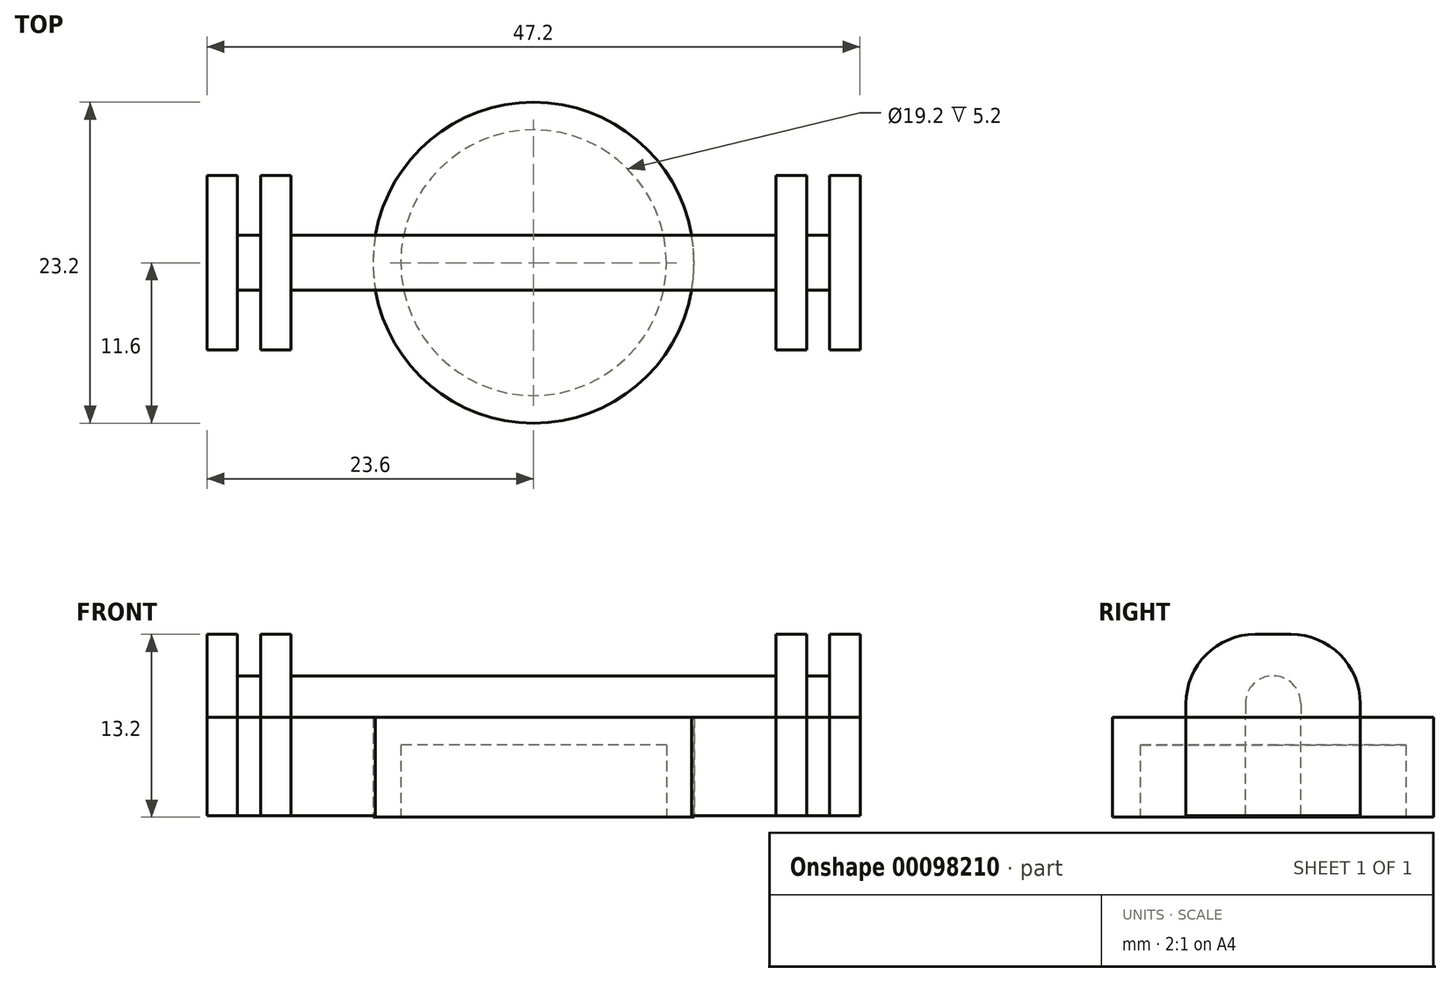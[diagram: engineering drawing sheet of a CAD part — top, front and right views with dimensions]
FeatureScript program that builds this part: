
annotation { "Feature Type Name" : "Feature", "Feature Type Description" : "" }
export const myFeature = defineFeature(function(context is Context, id is Id, definition is map)
    precondition{}
    {
        {
            var Q0;
            Q0=qCreatedBy(makeId("Top.planeOp"),FACE);
            var sketch = newSketch(context, id + "F0", { "sketchPlane" : qUnion([Q0])});
            skCircle(sketch, "E0", {"center": v(0, 0) * mm, "radius": 9.6 * mm});
            skCircle(sketch, "E1.0", {"center": v(0, 0) * mm, "radius": 11.6 * mm});
            skSolve(sketch);
        }
        {
            var Q0;
            Q0 = qSketchRegion(id + "F0", true);
            extrude(context, id + "F1", {"entities" : qUnion([Q0]), "depth" : 5.2 * mm});
        }
        {
            var Q0;
            Q0=makeQuery(id+"F1.opExtrude","CAP_FACE",FACE,{"disambiguationData":[OSD([sQuery(id+"F0.wireOp",EDGE,"E0"),sQuery(id+"F0.wireOp",EDGE,"E1.0")])],"isStart":false});
            var sketch = newSketch(context, id + "F2", { "sketchPlane" : qUnion([Q0])});
            skSolve(sketch);
        }
        {
            var Q0;
            Q0=makeQuery(id+"F2.imprint","IMPRINT",FACE,{"disambiguationData":[TD([[makeQuery(id+"F2.imprint","IMPRINT",EDGE,{"derivedFrom":makeQuery(id+"F1.opExtrude","CAP_EDGE",EDGE,{"disambiguationData":[OSD([sQuery(id+"F0.wireOp",EDGE,"E0")])],"isStart":false})}),1.0]])]});
            var Q1;
            Q1=makeQuery(id+"F2.imprint","IMPRINT",FACE,{"disambiguationData":[TD([[makeQuery(id+"F2.imprint","IMPRINT",EDGE,{"derivedFrom":makeQuery(id+"F1.opExtrude","CAP_EDGE",EDGE,{"disambiguationData":[OSD([sQuery(id+"F0.wireOp",EDGE,"E0")])],"isStart":false})}),-1.0]])]});
            extrude(context, id + "F3", {"entities" : qUnion([Q0, Q1]), "operationType" : NewBodyOperationType.ADD, "depth" : 2 * mm});
        }
        {
            var Q0;
            Q0=makeQuery(id+"F3.opExtrude","CAP_FACE",FACE,{"disambiguationData":[OSD([sQuery(id+"F0.wireOp",EDGE,"E1.0")])],"isStart":false});
            var sketch = newSketch(context, id + "F4", { "sketchPlane" : qUnion([Q0])});
            skLineSegment(sketch, "E2.bottom", {"start": v(-22.5, 2) * mm, "end": v(22.5, 2) * mm});
            skLineSegment(sketch, "E2.top", {"start": v(-22.5, -2) * mm, "end": v(22.5, -2) * mm});
            skLineSegment(sketch, "E2.left", {"start": v(-22.5, 2) * mm, "end": v(-22.5, -2) * mm});
            skLineSegment(sketch, "E2.right", {"start": v(22.5, 2) * mm, "end": v(22.5, -2) * mm});
            skPoint(sketch, "E2.middle", {"position": v(0, 0) * mm});
            skLineSegment(sketch, "E3.bottom", {"start": v(-21.4, -6.3) * mm, "end": v(-23.6, -6.3) * mm});
            skLineSegment(sketch, "E3.top", {"start": v(-21.4, 6.3) * mm, "end": v(-23.6, 6.3) * mm});
            skLineSegment(sketch, "E3.left", {"start": v(-21.4, -6.3) * mm, "end": v(-21.4, 6.3) * mm});
            skLineSegment(sketch, "E3.right", {"start": v(-23.6, -6.3) * mm, "end": v(-23.6, 6.3) * mm});
            skPoint(sketch, "E3.middle", {"position": v(-22.5, 0) * mm});
            skLineSegment(sketch, "E4.bottom", {"start": v(-17.53, 6.3) * mm, "end": v(-19.74, 6.3) * mm});
            skLineSegment(sketch, "E4.top", {"start": v(-17.53, -6.3) * mm, "end": v(-19.74, -6.3) * mm});
            skLineSegment(sketch, "E4.left", {"start": v(-17.53, 6.3) * mm, "end": v(-17.53, -6.3) * mm});
            skLineSegment(sketch, "E4.right", {"start": v(-19.74, 6.3) * mm, "end": v(-19.74, -6.3) * mm});
            skPoint(sketch, "E4.middle", {"position": v(-18.63, 0) * mm});
            skLineSegment(sketch, "E5.MirrorCS", {"start": v(23.6, -6.3) * mm, "end": v(23.6, 6.3) * mm});
            skLineSegment(sketch, "E6.MirrorCS", {"start": v(21.4, 6.3) * mm, "end": v(23.6, 6.3) * mm});
            skLineSegment(sketch, "E7.MirrorCS", {"start": v(21.4, -6.3) * mm, "end": v(21.4, 6.3) * mm});
            skLineSegment(sketch, "E8.MirrorCS", {"start": v(21.4, -6.3) * mm, "end": v(23.6, -6.3) * mm});
            skLineSegment(sketch, "E9.MirrorCS", {"start": v(19.74, 6.3) * mm, "end": v(19.74, -6.3) * mm});
            skLineSegment(sketch, "E10.MirrorCS", {"start": v(17.53, 6.3) * mm, "end": v(17.53, -6.3) * mm});
            skLineSegment(sketch, "E11.MirrorCS", {"start": v(17.53, -6.3) * mm, "end": v(19.74, -6.3) * mm});
            skLineSegment(sketch, "E12.MirrorCS", {"start": v(17.53, 6.3) * mm, "end": v(19.74, 6.3) * mm});
            skSolve(sketch);
        }
        {
            var Q0;
            {var subQ0=sQuery(id+"F4.wireOp",EDGE,"E4.left");var subQ1=sQuery(id+"F4.wireOp",EDGE,"E2.bottom");var subQ2=makeQuery(id+"F4.imprint","INTERSECT",VERTEX,{"derivedFrom":[subQ1,subQ0]});Q0=makeQuery(id+"F4.imprint","IMPRINT",FACE,{"disambiguationData":[TD([[makeQuery(id+"F4.imprint","IMPRINT",EDGE,{"disambiguationData":[TD([[subQ2,-1.0]])],"derivedFrom":subQ1}),-1.0]])]});}
            var Q1;
            {var subQ0=sQuery(id+"F4.wireOp",EDGE,"E4.right");var subQ1=sQuery(id+"F4.wireOp",EDGE,"E2.bottom");var subQ2=makeQuery(id+"F4.imprint","INTERSECT",VERTEX,{"derivedFrom":[subQ1,subQ0]});Q1=makeQuery(id+"F4.imprint","IMPRINT",FACE,{"disambiguationData":[TD([[makeQuery(id+"F4.imprint","IMPRINT",EDGE,{"disambiguationData":[TD([[subQ2,-1.0]])],"derivedFrom":subQ1}),-1.0]])]});}
            var Q2;
            {var subQ5=sQuery(id+"F4.wireOp",EDGE,"E4.top");Q2=makeQuery(id+"F4.imprint","IMPRINT",FACE,{"disambiguationData":[TD([[makeQuery(id+"F4.imprint","IMPRINT",EDGE,{"derivedFrom":subQ5}),-1.0]])]});}
            var Q3;
            {var subQ1=sQuery(id+"F4.wireOp",EDGE,"E2.left");Q3=makeQuery(id+"F4.imprint","IMPRINT",FACE,{"disambiguationData":[TD([[makeQuery(id+"F4.imprint","IMPRINT",EDGE,{"derivedFrom":subQ1}),-1.0]])]});}
            var Q4;
            {var subQ0=sQuery(id+"F4.wireOp",EDGE,"E2.left");Q4=makeQuery(id+"F4.imprint","IMPRINT",FACE,{"disambiguationData":[TD([[makeQuery(id+"F4.imprint","IMPRINT",EDGE,{"derivedFrom":subQ0}),1.0]])]});}
            var Q5;
            {var subQ5=sQuery(id+"F4.wireOp",EDGE,"E4.bottom");Q5=makeQuery(id+"F4.imprint","IMPRINT",FACE,{"disambiguationData":[TD([[makeQuery(id+"F4.imprint","IMPRINT",EDGE,{"derivedFrom":subQ5}),1.0]])]});}
            var Q6;
            {var subQ0=sQuery(id+"F4.wireOp",EDGE,"E3.left");var subQ1=sQuery(id+"F4.wireOp",EDGE,"E2.bottom");var subQ2=makeQuery(id+"F4.imprint","INTERSECT",VERTEX,{"derivedFrom":[subQ1,subQ0]});Q6=makeQuery(id+"F4.imprint","IMPRINT",FACE,{"disambiguationData":[TD([[makeQuery(id+"F4.imprint","IMPRINT",EDGE,{"disambiguationData":[TD([[subQ2,-1.0]])],"derivedFrom":subQ1}),-1.0]])]});}
            var Q7;
            {var subQ0=sQuery(id+"F4.wireOp",EDGE,"E10.MirrorCS");var subQ1=sQuery(id+"F4.wireOp",EDGE,"E2.bottom");var subQ2=makeQuery(id+"F4.imprint","INTERSECT",VERTEX,{"derivedFrom":[subQ1,subQ0]});Q7=makeQuery(id+"F4.imprint","IMPRINT",FACE,{"disambiguationData":[TD([[makeQuery(id+"F4.imprint","IMPRINT",EDGE,{"disambiguationData":[TD([[subQ2,1.0]])],"derivedFrom":subQ1}),-1.0]])]});}
            var Q8;
            {var subQ0=sQuery(id+"F4.wireOp",EDGE,"E10.MirrorCS");var subQ1=sQuery(id+"F4.wireOp",EDGE,"E2.bottom");var subQ2=makeQuery(id+"F4.imprint","INTERSECT",VERTEX,{"derivedFrom":[subQ1,subQ0]});Q8=makeQuery(id+"F4.imprint","IMPRINT",FACE,{"disambiguationData":[TD([[makeQuery(id+"F4.imprint","IMPRINT",EDGE,{"disambiguationData":[TD([[subQ2,-1.0]])],"derivedFrom":subQ1}),-1.0]])]});}
            var Q9;
            {var subQ5=sQuery(id+"F4.wireOp",EDGE,"E11.MirrorCS");Q9=makeQuery(id+"F4.imprint","IMPRINT",FACE,{"disambiguationData":[TD([[makeQuery(id+"F4.imprint","IMPRINT",EDGE,{"derivedFrom":subQ5}),1.0]])]});}
            var Q10;
            {var subQ0=sQuery(id+"F4.wireOp",EDGE,"E2.right");Q10=makeQuery(id+"F4.imprint","IMPRINT",FACE,{"disambiguationData":[TD([[makeQuery(id+"F4.imprint","IMPRINT",EDGE,{"derivedFrom":subQ0}),1.0]])]});}
            var Q11;
            {var subQ0=sQuery(id+"F4.wireOp",EDGE,"E9.MirrorCS");var subQ1=sQuery(id+"F4.wireOp",EDGE,"E2.bottom");var subQ2=makeQuery(id+"F4.imprint","INTERSECT",VERTEX,{"derivedFrom":[subQ1,subQ0]});Q11=makeQuery(id+"F4.imprint","IMPRINT",FACE,{"disambiguationData":[TD([[makeQuery(id+"F4.imprint","IMPRINT",EDGE,{"disambiguationData":[TD([[subQ2,-1.0]])],"derivedFrom":subQ1}),-1.0]])]});}
            var Q12;
            {var subQ5=sQuery(id+"F4.wireOp",EDGE,"E12.MirrorCS");Q12=makeQuery(id+"F4.imprint","IMPRINT",FACE,{"disambiguationData":[TD([[makeQuery(id+"F4.imprint","IMPRINT",EDGE,{"derivedFrom":subQ5}),-1.0]])]});}
            var Q13;
            {var subQ0=sQuery(id+"F4.wireOp",EDGE,"E2.right");Q13=makeQuery(id+"F4.imprint","IMPRINT",FACE,{"disambiguationData":[TD([[makeQuery(id+"F4.imprint","IMPRINT",EDGE,{"derivedFrom":subQ0}),-1.0]])]});}
            extrude(context, id + "F5", {"entities" : qUnion([Q0, Q1, Q2, Q3, Q4, Q5, Q6, Q7, Q8, Q9, Q10, Q11, Q12, Q13]), "oppositeDirection" : true, "depth" : 7.1 * mm});
        }
        {
            var Q0;
            {var subQ0=sQuery(id+"F4.wireOp",EDGE,"E4.left");var subQ1=sQuery(id+"F4.wireOp",EDGE,"E2.bottom");var subQ2=makeQuery(id+"F4.imprint","INTERSECT",VERTEX,{"derivedFrom":[subQ1,subQ0]});Q0=makeQuery(id+"F4.imprint","IMPRINT",FACE,{"disambiguationData":[TD([[makeQuery(id+"F4.imprint","IMPRINT",EDGE,{"disambiguationData":[TD([[subQ2,-1.0]])],"derivedFrom":subQ1}),-1.0]])]});}
            var Q1;
            {var subQ0=sQuery(id+"F4.wireOp",EDGE,"E3.left");var subQ1=sQuery(id+"F4.wireOp",EDGE,"E2.bottom");var subQ2=makeQuery(id+"F4.imprint","INTERSECT",VERTEX,{"derivedFrom":[subQ1,subQ0]});Q1=makeQuery(id+"F4.imprint","IMPRINT",FACE,{"disambiguationData":[TD([[makeQuery(id+"F4.imprint","IMPRINT",EDGE,{"disambiguationData":[TD([[subQ2,-1.0]])],"derivedFrom":subQ1}),-1.0]])]});}
            var Q2;
            {var subQ0=sQuery(id+"F4.wireOp",EDGE,"E2.bottom");var subQ1=makeQuery(id+"F3.opExtrude","CAP_EDGE",EDGE,{"disambiguationData":[OSD([sQuery(id+"F0.wireOp",EDGE,"E1.0")])],"isStart":false});var subQ2=makeQuery(id+"F4.imprint","INTERSECT",VERTEX,{"disambiguationData":[OD(0.0)],"derivedFrom":[subQ1,subQ0]});Q2=makeQuery(id+"F4.imprint","IMPRINT",FACE,{"disambiguationData":[TD([[makeQuery(id+"F4.imprint","IMPRINT",EDGE,{"disambiguationData":[TD([[subQ2,-1.0]])],"derivedFrom":subQ0}),-1.0]])]});}
            var Q3;
            {var subQ0=sQuery(id+"F4.wireOp",EDGE,"E10.MirrorCS");var subQ1=sQuery(id+"F4.wireOp",EDGE,"E2.bottom");var subQ2=makeQuery(id+"F4.imprint","INTERSECT",VERTEX,{"derivedFrom":[subQ1,subQ0]});Q3=makeQuery(id+"F4.imprint","IMPRINT",FACE,{"disambiguationData":[TD([[makeQuery(id+"F4.imprint","IMPRINT",EDGE,{"disambiguationData":[TD([[subQ2,1.0]])],"derivedFrom":subQ1}),-1.0]])]});}
            var Q4;
            {var subQ0=sQuery(id+"F4.wireOp",EDGE,"E9.MirrorCS");var subQ1=sQuery(id+"F4.wireOp",EDGE,"E2.bottom");var subQ2=makeQuery(id+"F4.imprint","INTERSECT",VERTEX,{"derivedFrom":[subQ1,subQ0]});Q4=makeQuery(id+"F4.imprint","IMPRINT",FACE,{"disambiguationData":[TD([[makeQuery(id+"F4.imprint","IMPRINT",EDGE,{"disambiguationData":[TD([[subQ2,-1.0]])],"derivedFrom":subQ1}),-1.0]])]});}
            extrude(context, id + "F6", {"entities" : qUnion([Q0, Q1, Q2, Q3, Q4]), "depth" : 3 * mm});
        }
        {
            var Q0;
            {var subQ1=sQuery(id+"F4.wireOp",EDGE,"E2.left");Q0=makeQuery(id+"F4.imprint","IMPRINT",FACE,{"disambiguationData":[TD([[makeQuery(id+"F4.imprint","IMPRINT",EDGE,{"derivedFrom":subQ1}),-1.0]])]});}
            var Q1;
            {var subQ0=sQuery(id+"F4.wireOp",EDGE,"E2.left");Q1=makeQuery(id+"F4.imprint","IMPRINT",FACE,{"disambiguationData":[TD([[makeQuery(id+"F4.imprint","IMPRINT",EDGE,{"derivedFrom":subQ0}),1.0]])]});}
            var Q2;
            {var subQ5=sQuery(id+"F4.wireOp",EDGE,"E4.bottom");Q2=makeQuery(id+"F4.imprint","IMPRINT",FACE,{"disambiguationData":[TD([[makeQuery(id+"F4.imprint","IMPRINT",EDGE,{"derivedFrom":subQ5}),1.0]])]});}
            var Q3;
            {var subQ0=sQuery(id+"F4.wireOp",EDGE,"E4.right");var subQ1=sQuery(id+"F4.wireOp",EDGE,"E2.bottom");var subQ2=makeQuery(id+"F4.imprint","INTERSECT",VERTEX,{"derivedFrom":[subQ1,subQ0]});Q3=makeQuery(id+"F4.imprint","IMPRINT",FACE,{"disambiguationData":[TD([[makeQuery(id+"F4.imprint","IMPRINT",EDGE,{"disambiguationData":[TD([[subQ2,-1.0]])],"derivedFrom":subQ1}),-1.0]])]});}
            var Q4;
            {var subQ5=sQuery(id+"F4.wireOp",EDGE,"E4.top");Q4=makeQuery(id+"F4.imprint","IMPRINT",FACE,{"disambiguationData":[TD([[makeQuery(id+"F4.imprint","IMPRINT",EDGE,{"derivedFrom":subQ5}),-1.0]])]});}
            var Q5;
            {var subQ5=sQuery(id+"F4.wireOp",EDGE,"E12.MirrorCS");Q5=makeQuery(id+"F4.imprint","IMPRINT",FACE,{"disambiguationData":[TD([[makeQuery(id+"F4.imprint","IMPRINT",EDGE,{"derivedFrom":subQ5}),-1.0]])]});}
            var Q6;
            {var subQ0=sQuery(id+"F4.wireOp",EDGE,"E10.MirrorCS");var subQ1=sQuery(id+"F4.wireOp",EDGE,"E2.bottom");var subQ2=makeQuery(id+"F4.imprint","INTERSECT",VERTEX,{"derivedFrom":[subQ1,subQ0]});Q6=makeQuery(id+"F4.imprint","IMPRINT",FACE,{"disambiguationData":[TD([[makeQuery(id+"F4.imprint","IMPRINT",EDGE,{"disambiguationData":[TD([[subQ2,-1.0]])],"derivedFrom":subQ1}),-1.0]])]});}
            var Q7;
            {var subQ5=sQuery(id+"F4.wireOp",EDGE,"E11.MirrorCS");Q7=makeQuery(id+"F4.imprint","IMPRINT",FACE,{"disambiguationData":[TD([[makeQuery(id+"F4.imprint","IMPRINT",EDGE,{"derivedFrom":subQ5}),1.0]])]});}
            var Q8;
            {var subQ0=sQuery(id+"F4.wireOp",EDGE,"E2.right");Q8=makeQuery(id+"F4.imprint","IMPRINT",FACE,{"disambiguationData":[TD([[makeQuery(id+"F4.imprint","IMPRINT",EDGE,{"derivedFrom":subQ0}),1.0]])]});}
            var Q9;
            {var subQ0=sQuery(id+"F4.wireOp",EDGE,"E2.right");Q9=makeQuery(id+"F4.imprint","IMPRINT",FACE,{"disambiguationData":[TD([[makeQuery(id+"F4.imprint","IMPRINT",EDGE,{"derivedFrom":subQ0}),-1.0]])]});}
            extrude(context, id + "F7", {"entities" : qUnion([Q0, Q1, Q2, Q3, Q4, Q5, Q6, Q7, Q8, Q9]), "depth" : 6 * mm});
        }
        {
            var Q0;
            Q0=makeQuery(id+"F7.opExtrude","CAP_EDGE",EDGE,{"disambiguationData":[OSD([sQuery(id+"F4.wireOp",EDGE,"E3.top")])],"isStart":false});
            var Q1;
            Q1=makeQuery(id+"F7.opExtrude","CAP_EDGE",EDGE,{"disambiguationData":[OSD([sQuery(id+"F4.wireOp",EDGE,"E4.bottom")])],"isStart":false});
            var Q2;
            Q2=makeQuery(id+"F7.opExtrude","CAP_EDGE",EDGE,{"disambiguationData":[OSD([sQuery(id+"F4.wireOp",EDGE,"E3.bottom")])],"isStart":false});
            var Q3;
            Q3=makeQuery(id+"F7.opExtrude","CAP_EDGE",EDGE,{"disambiguationData":[OSD([sQuery(id+"F4.wireOp",EDGE,"E4.top")])],"isStart":false});
            var Q4;
            Q4=makeQuery(id+"F7.opExtrude","CAP_EDGE",EDGE,{"disambiguationData":[OSD([sQuery(id+"F4.wireOp",EDGE,"E11.MirrorCS")])],"isStart":false});
            var Q5;
            Q5=makeQuery(id+"F7.opExtrude","CAP_EDGE",EDGE,{"disambiguationData":[OSD([sQuery(id+"F4.wireOp",EDGE,"E8.MirrorCS")])],"isStart":false});
            var Q6;
            Q6=makeQuery(id+"F7.opExtrude","CAP_EDGE",EDGE,{"disambiguationData":[OSD([sQuery(id+"F4.wireOp",EDGE,"E6.MirrorCS")])],"isStart":false});
            var Q7;
            Q7=makeQuery(id+"F7.opExtrude","CAP_EDGE",EDGE,{"disambiguationData":[OSD([sQuery(id+"F4.wireOp",EDGE,"E12.MirrorCS")])],"isStart":false});
            fillet(context, id + "F8", {"entities" : qUnion([Q0, Q1, Q2, Q3, Q4, Q5, Q6, Q7]), "radius" : 5 * mm, "tangentPropagation" : true, "allowEdgeOverflow" : false});
        }
        {
            var Q0;
            {var subQ0=sQuery(id+"F4.wireOp",EDGE,"E2.top");var subQ1=makeQuery(id+"F3.opExtrude","CAP_EDGE",EDGE,{"disambiguationData":[OSD([sQuery(id+"F0.wireOp",EDGE,"E1.0")])],"isStart":false});var subQ3=makeQuery(id+"F4.imprint","INTERSECT",VERTEX,{"disambiguationData":[OD(0.0)],"derivedFrom":[subQ1,subQ0]});Q0=makeQuery(id+"F6.opExtrude","CAP_EDGE",EDGE,{"disambiguationData":[OSD([subQ0]),TDD([makeQuery(id+"F4.imprint","IMPRINT",EDGE,{"disambiguationData":[TD([[makeQuery(id+"F4.imprint","INTERSECT",VERTEX,{"derivedFrom":[subQ0,sQuery(id+"F4.wireOp",EDGE,"E4.left")]}),-1.0]])],"derivedFrom":subQ0}),makeQuery(id+"F4.imprint","IMPRINT",EDGE,{"disambiguationData":[TD([[subQ3,-1.0]])],"derivedFrom":subQ0}),makeQuery(id+"F4.imprint","IMPRINT",EDGE,{"disambiguationData":[TD([[makeQuery(id+"F4.imprint","INTERSECT",VERTEX,{"derivedFrom":[subQ0,sQuery(id+"F4.wireOp",EDGE,"E10.MirrorCS")]}),1.0]])],"derivedFrom":subQ0})])],"isStart":false});}
            var Q1;
            {var subQ0=sQuery(id+"F4.wireOp",EDGE,"E2.bottom");var subQ1=makeQuery(id+"F3.opExtrude","CAP_EDGE",EDGE,{"disambiguationData":[OSD([sQuery(id+"F0.wireOp",EDGE,"E1.0")])],"isStart":false});var subQ3=makeQuery(id+"F4.imprint","INTERSECT",VERTEX,{"disambiguationData":[OD(0.0)],"derivedFrom":[subQ1,subQ0]});Q1=makeQuery(id+"F6.opExtrude","CAP_EDGE",EDGE,{"disambiguationData":[OSD([subQ0]),TDD([makeQuery(id+"F4.imprint","IMPRINT",EDGE,{"disambiguationData":[TD([[makeQuery(id+"F4.imprint","INTERSECT",VERTEX,{"derivedFrom":[subQ0,sQuery(id+"F4.wireOp",EDGE,"E4.left")]}),-1.0]])],"derivedFrom":subQ0}),makeQuery(id+"F4.imprint","IMPRINT",EDGE,{"disambiguationData":[TD([[subQ3,-1.0]])],"derivedFrom":subQ0}),makeQuery(id+"F4.imprint","IMPRINT",EDGE,{"disambiguationData":[TD([[makeQuery(id+"F4.imprint","INTERSECT",VERTEX,{"derivedFrom":[subQ0,sQuery(id+"F4.wireOp",EDGE,"E10.MirrorCS")]}),1.0]])],"derivedFrom":subQ0})])],"isStart":false});}
            var Q2;
            {var subQ0=sQuery(id+"F4.wireOp",EDGE,"E2.top");Q2=makeQuery(id+"F6.opExtrude","CAP_EDGE",EDGE,{"disambiguationData":[OSD([subQ0]),TDD([makeQuery(id+"F4.imprint","IMPRINT",EDGE,{"disambiguationData":[TD([[makeQuery(id+"F4.imprint","INTERSECT",VERTEX,{"derivedFrom":[subQ0,sQuery(id+"F4.wireOp",EDGE,"E9.MirrorCS")]}),-1.0]])],"derivedFrom":subQ0})])],"isStart":false});}
            var Q3;
            {var subQ0=sQuery(id+"F4.wireOp",EDGE,"E2.bottom");Q3=makeQuery(id+"F6.opExtrude","CAP_EDGE",EDGE,{"disambiguationData":[OSD([subQ0]),TDD([makeQuery(id+"F4.imprint","IMPRINT",EDGE,{"disambiguationData":[TD([[makeQuery(id+"F4.imprint","INTERSECT",VERTEX,{"derivedFrom":[subQ0,sQuery(id+"F4.wireOp",EDGE,"E9.MirrorCS")]}),-1.0]])],"derivedFrom":subQ0})])],"isStart":false});}
            var Q4;
            {var subQ0=sQuery(id+"F4.wireOp",EDGE,"E2.top");Q4=makeQuery(id+"F6.opExtrude","CAP_EDGE",EDGE,{"disambiguationData":[OSD([subQ0]),TDD([makeQuery(id+"F4.imprint","IMPRINT",EDGE,{"disambiguationData":[TD([[makeQuery(id+"F4.imprint","INTERSECT",VERTEX,{"derivedFrom":[subQ0,sQuery(id+"F4.wireOp",EDGE,"E3.left")]}),-1.0]])],"derivedFrom":subQ0})])],"isStart":false});}
            var Q5;
            {var subQ0=sQuery(id+"F4.wireOp",EDGE,"E2.bottom");Q5=makeQuery(id+"F6.opExtrude","CAP_EDGE",EDGE,{"disambiguationData":[OSD([subQ0]),TDD([makeQuery(id+"F4.imprint","IMPRINT",EDGE,{"disambiguationData":[TD([[makeQuery(id+"F4.imprint","INTERSECT",VERTEX,{"derivedFrom":[subQ0,sQuery(id+"F4.wireOp",EDGE,"E3.left")]}),-1.0]])],"derivedFrom":subQ0})])],"isStart":false});}
            fillet(context, id + "F9", {"entities" : qUnion([Q0, Q1, Q2, Q3, Q4, Q5]), "radius" : 2 * mm, "tangentPropagation" : true, "allowEdgeOverflow" : false});
        }
    });
